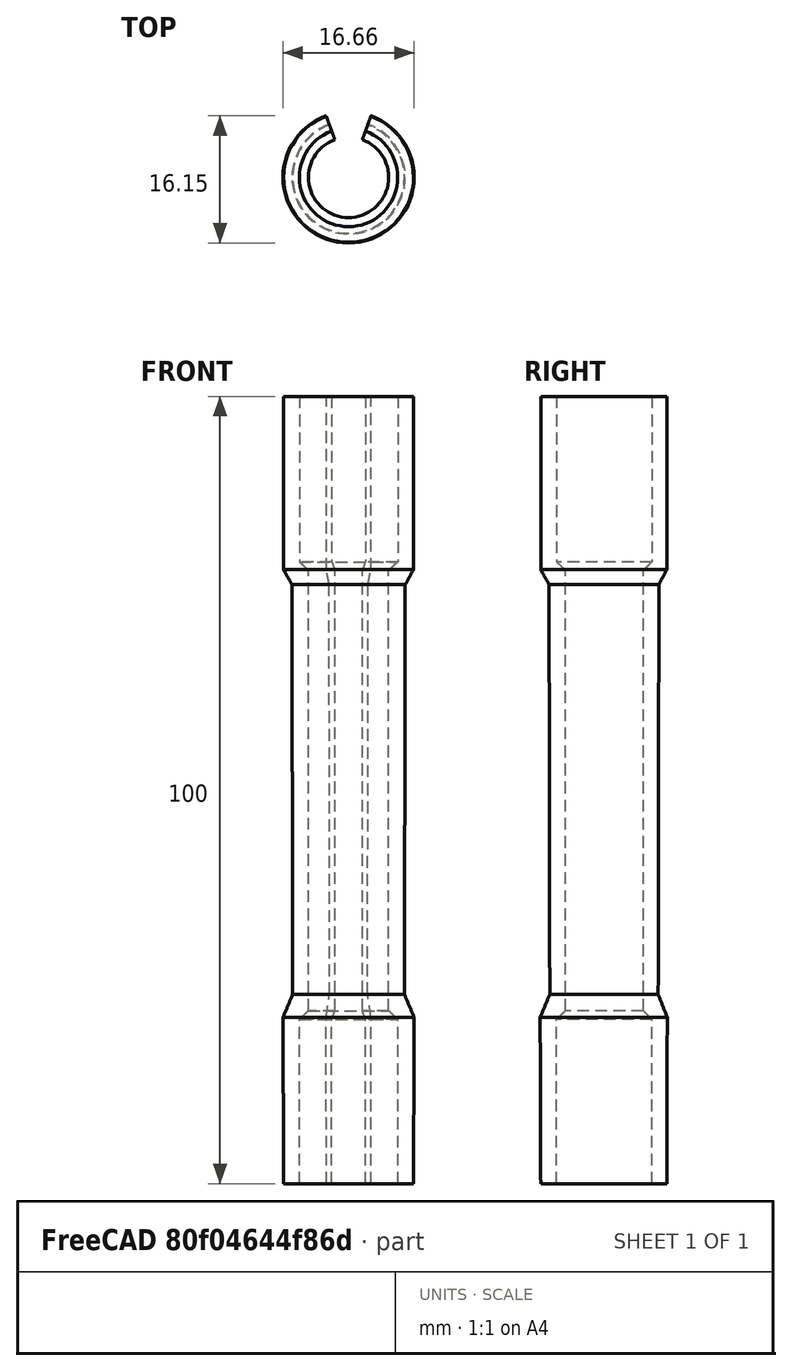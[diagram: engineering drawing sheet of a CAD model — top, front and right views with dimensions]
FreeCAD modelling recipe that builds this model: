
FCSTD DOCUMENT  (FreeCAD 0.19R20514 (Git))
Label: VerticalSlider
License: All rights reserved
LicenseURL: http://en.wikipedia.org/wiki/All_rights_reserved
objects: Sketcher::SketchObject×1, PartDesign::Revolution×1, PartDesign::Body×1
note: 4 computed .brp shape members not serialized (recipe doc carries the construction recipe); baked Part::Feature solids carry a one-line shape summary decoded from their .brp

FEATURE [Sketcher::SketchObject] Sketch
  MapMode = 5
  Placement = pos=(0,0,0) rot=(1,0,0;1.5708rad)
  Support = -> [XZ_Plane]
  sketch-geometry (13):
    g0: BSplineCurve PolesCount=2 KnotsCount=2 Degree=1 IsPeriodic=0
    g1: BSplineCurve PolesCount=2 KnotsCount=2 Degree=1 IsPeriodic=0
    g2: BSplineCurve PolesCount=2 KnotsCount=2 Degree=1 IsPeriodic=0
    g3: BSplineCurve PolesCount=2 KnotsCount=2 Degree=1 IsPeriodic=0
    g4: BSplineCurve PolesCount=2 KnotsCount=2 Degree=1 IsPeriodic=0
    g5: BSplineCurve PolesCount=2 KnotsCount=2 Degree=1 IsPeriodic=0
    g6: BSplineCurve PolesCount=2 KnotsCount=2 Degree=1 IsPeriodic=0
    g7: LineSegment StartX=-5.1 StartY=77.9321 StartZ=0 EndX=-5.19131 EndY=77.9321 EndZ=0
    g8: BSplineCurve PolesCount=2 KnotsCount=2 Degree=1 IsPeriodic=0
    g9: BSplineCurve PolesCount=2 KnotsCount=2 Degree=1 IsPeriodic=0
    g10: BSplineCurve PolesCount=2 KnotsCount=2 Degree=1 IsPeriodic=0
    g11: BSplineCurve PolesCount=2 KnotsCount=2 Degree=1 IsPeriodic=0
    g12: BSplineCurve PolesCount=2 KnotsCount=2 Degree=1 IsPeriodic=0
  constraints (24):
    c: Coincident(g0,g1)
    c: Coincident(g1,g2)
    c: Coincident(g2,g3)
    c: Coincident(g0,g4)
    c: Coincident(g4,g5)
    c: Coincident(g5,g6)
    c: Coincident(g6,g7)
    c: Horizontal(g7)
    c: Coincident(g3,g8)
    c: Coincident(g8,g9)
    c: Coincident(g9,g10)
    c: Coincident(g10,g11)
    c: Coincident(g11,g12)
    c: Coincident(g12,g6)
    c: DistanceX(g0,g0) = 2
    c: DistanceX(g0,g-1) = 6.25
    c: DistanceX(g4,g-1) = 6.25
    c: DistanceX(g5,g-1) = 5.1
    c: DistanceX(g2,g5) = 2
    c: DistanceX(g3,g7) = 2
    c: DistanceX(g8,g11) = 2
    c: DistanceX(g-2,g11) = -6.25
    c: DistanceX(g-2,g10) = -6.25
    c: DistanceX(g9,g10) = 2
FEATURE [PartDesign::Revolution] Revolution
  Angle = 320
  Axis = (-3e-16,3e-16,1)
  Base = (0,0,0)
  Midplane = true
  Placement = pos=(0,0,0) rot=(1,0,0;1.5708rad)
  Profile = -> Sketch
  ReferenceAxis = -> Z_Axis
FEATURE [PartDesign::Body] Body  label="Bearingholder"
  Group = -> [Sketch,Revolution]
  Origin = -> Origin
  Placement = pos=(0,0,0) rot=(0,0,1;1.5708rad)
  Tip = -> Revolution
